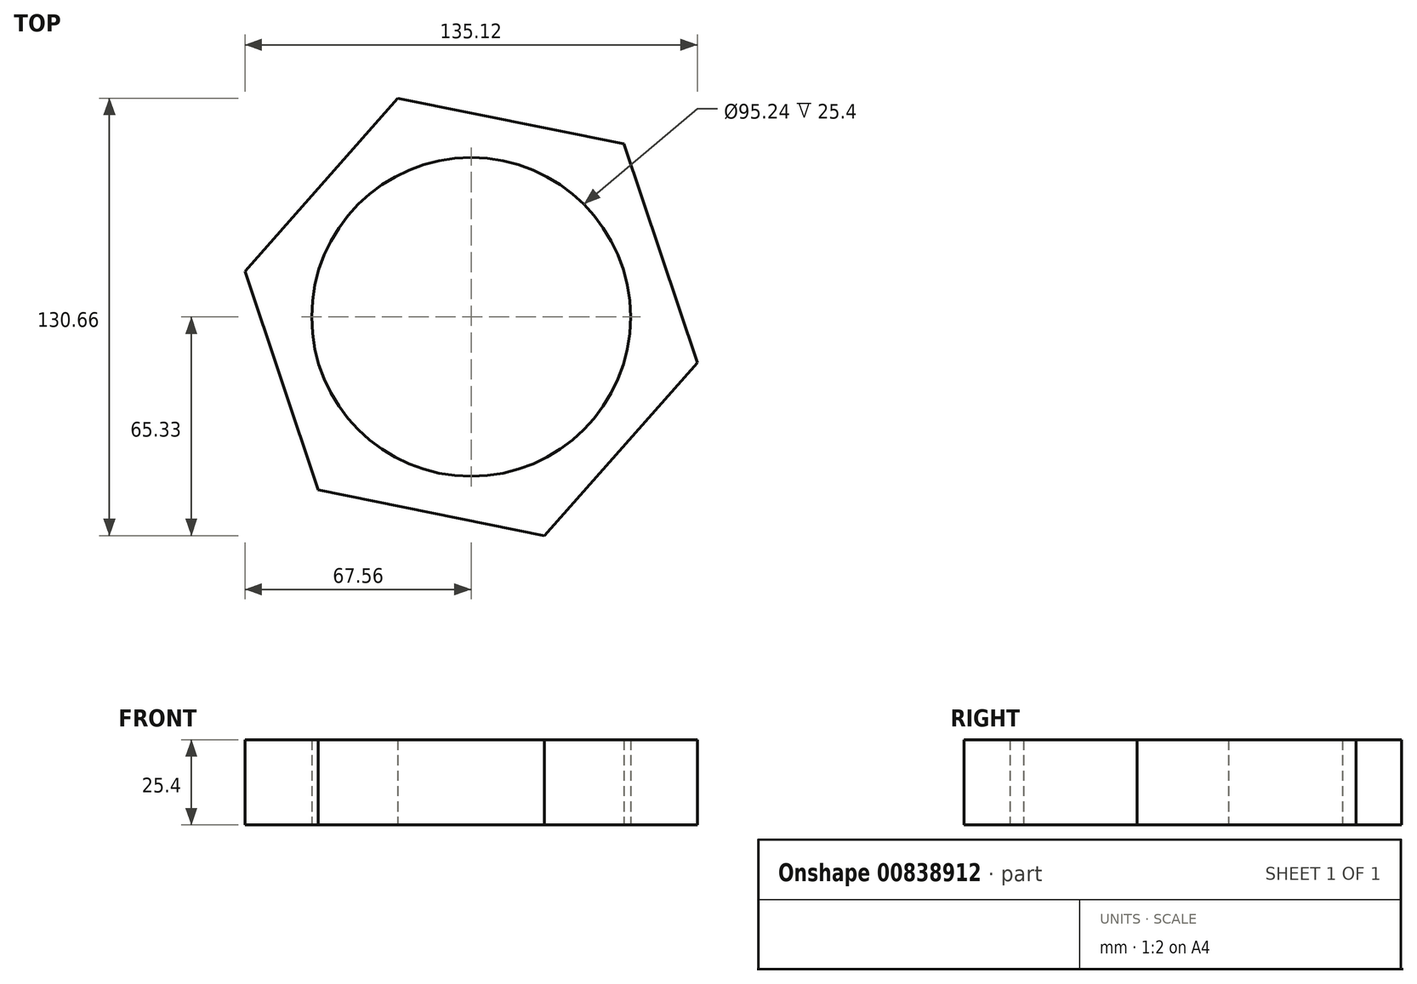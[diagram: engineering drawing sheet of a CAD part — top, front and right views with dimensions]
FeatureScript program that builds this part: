
annotation { "Feature Type Name" : "Feature", "Feature Type Description" : "" }
export const myFeature = defineFeature(function(context is Context, id is Id, definition is map)
    precondition{}
    {
        {
            var Q0;
            Q0=qCreatedBy(makeId("Top.planeOp"),FACE);
            var sketch = newSketch(context, id + "F0", { "sketchPlane" : qUnion([Q0])});
            skCircle(sketch, "E0.cCircle", {"center": v(0, 0) * mm, "radius": 59.69 * mm, "construction": true});
            skLineSegment(sketch, "E0.0", {"start": v(67.56, -13.66) * mm, "end": v(21.95, -65.33) * mm});
            skLineSegment(sketch, "E0.1", {"start": v(21.95, -65.33) * mm, "end": v(-45.6, -51.68) * mm});
            skLineSegment(sketch, "E0.2", {"start": v(-45.6, -51.68) * mm, "end": v(-67.56, 13.66) * mm});
            skLineSegment(sketch, "E0.3", {"start": v(-67.56, 13.66) * mm, "end": v(-21.95, 65.33) * mm});
            skLineSegment(sketch, "E0.4", {"start": v(-21.95, 65.33) * mm, "end": v(45.6, 51.68) * mm});
            skLineSegment(sketch, "E0.5", {"start": v(45.6, 51.68) * mm, "end": v(67.56, -13.66) * mm});
            skPoint(sketch, "E0.0.midPoint", {"position": v(44.75, -39.5) * mm});
            skCircle(sketch, "E1", {"center": v(0, 0) * mm, "radius": 47.62 * mm});
            skSolve(sketch);
        }
        {
            var Q0;
            Q0 = qSketchRegion(id + "F0", true);
            extrude(context, id + "F1", {"entities" : qUnion([Q0]), "depth" : 25.4 * mm, "offsetDistance" : 25.4 * mm});
        }
    });
